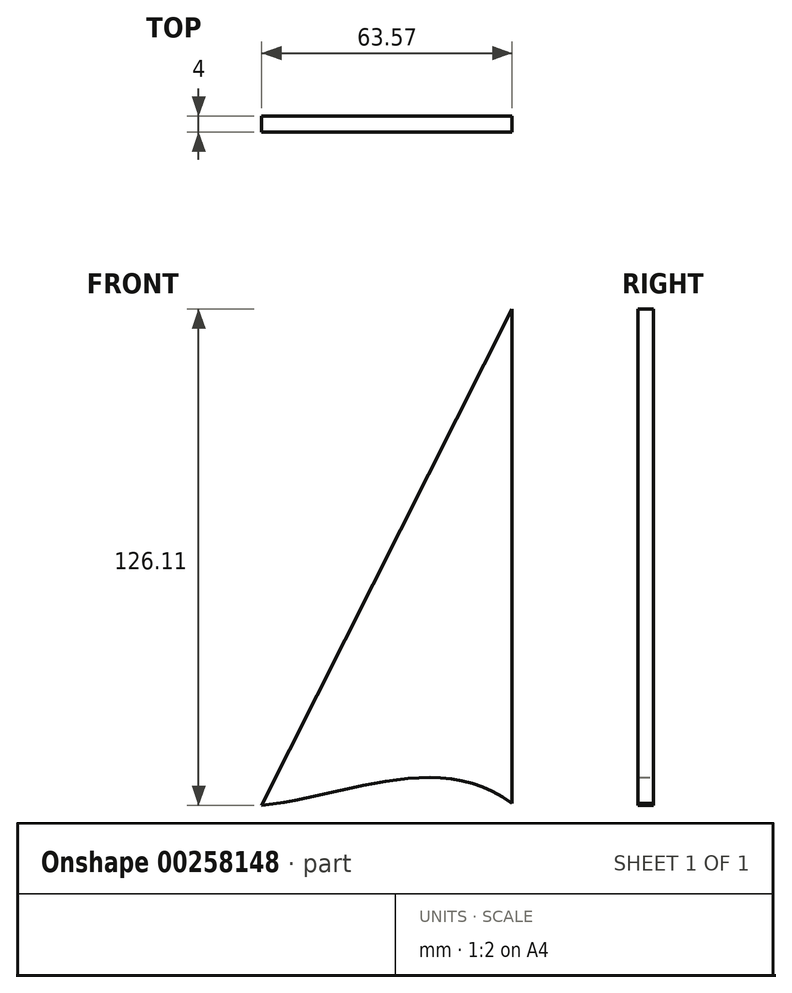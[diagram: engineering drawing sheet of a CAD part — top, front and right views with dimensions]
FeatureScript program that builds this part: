
annotation { "Feature Type Name" : "Feature", "Feature Type Description" : "" }
export const myFeature = defineFeature(function(context is Context, id is Id, definition is map)
    precondition{}
    {
        {
            var Q0;
            Q0=qCreatedBy(makeId("Front.planeOp"),FACE);
            var sketch = newSketch(context, id + "F0", { "sketchPlane" : qUnion([Q0])});
            skLineSegment(sketch, "E0", {"start": v(0, 60.46) * mm, "end": v(0, -65.12) * mm});
            skLineSegment(sketch, "E1", {"start": v(0, 60.46) * mm, "end": v(-63.57, -65.65) * mm});
            skFitSpline(sketch, "E2", {"points": [v(-63.57, -65.65) * mm, v(0, -65.12) * mm], "startDerivative": vector(64.56, 6.6) * mm, "endDerivative": vector(55.61, -41.59) * mm});
            skSolve(sketch);
        }
        {
            var Q0;
            Q0 = qSketchRegion(id + "F0", true);
            extrude(context, id + "F1", {"entities" : qUnion([Q0]), "depth" : 4 * mm});
        }
    });
